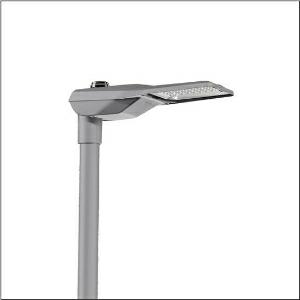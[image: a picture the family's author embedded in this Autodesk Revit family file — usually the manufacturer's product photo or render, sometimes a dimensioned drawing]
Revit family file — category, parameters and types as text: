
# Revit family: streetlight_sl_21_mini___st1_0a_5xe6d47n08gb_0bcc
name_source: partatom
category: Lighting Fixtures
units: mm (PartAtom-declared; Revit-internal decimal feet)

## family parameters
Cut with Voids When Loaded = No
Host = Face
Light Source = No
Part Type = Normal
Room Calculation Point = No
Round Connector Dimension = Use Diameter
Shared = No

## types (1)
- --- (1 x LED, 6180 lm, 40.4 W, 4000K)
    Apparent Load = 40 VA
    CIE Flux Codes = 37 72 97 100 100
    Color Rendering = 70
    Color Temperature = 4000K
    Default Elevation = 1800 mm
    Description = Streetlight SL 21 mini, mast luminaire, primary light control with lens, of PMMA, primary optical cover: cover, of toughened safety glass, transparent, light distribution: ST1.0a, light emission: direct distribution, primary light characteristic: asymmetric, installation type: side-entry, LED, 3G 1.5mm², High Power LED, rated luminous flux: 6.180lm, luminous efficacy: 153lm/W, light colour: 740, colour temperature: 4000K, control gear: NEMA (7pin), control: overheat protection, pre-setting: linear dimming characteristic, constant luminous flux control, time-dependent luminous flux control, flexible luminous flux parameterisation, mains connection: 230..240V, AC, 50/60Hz, connection cable pre-assembled, cable length: 8,5m, wiring characteristics: H07RN-F, start of lifetime: 40W, end of service life: 41W, reduction: 19W, luminaire housing, of diecast aluminium (EN AC-44300), powder-coated, Siteco® metallic grey (DB 702S), corrosivity category C5 mid according to DIN EN ISO 12944, multi-level sealing system, sealing non-destructively replaceable, inclination adjustable: 0°, 5°, 10°, 15°, length: 628mm, width: 235mm, height: 110mm, spigot size: 42mm (side-entry), mounting height: 4..8m, protection rating (complete): IP66, insulation class (complete): insulation class I (protective earthing), certification: CE, ENEC, ENEC+, VDE, impact resistance: IK10, permissible operating ambient temperature for outdoor applications: -40..+50°C, standard-compliant lighting for roads and squares, packaging unit: 1 piece

Light Distribution: ST1.0a
    Height = 110 mm
    Lamp = 1 x LED
    Lamp Light Flux = 6180 lm
    Lamp Power = 40.4 W
    Lamp count = 1
    Length = 625 mm
    Luminous efficacy = 153 lm/W
    Manufacturer = Siteco
    ModVariant = No
    Model = 5XE6D47N08GB
    Number of Poles = 1
    OnlyDefault = Yes
    Power Factor = 1
    Product Name = Streetlight SL 21 mini | ST1.0a
    Product group = mast luminaire | pylon top
    ProductGroupID = 6100
    Protection Class = Protection class I
    Protection Degree = IP 66
    RLX_Detail_Level = 1
    RLX_Emergency_Light_Flux = 0 lm
    RLX_Emergency_Type = 0
    RLX_Emergency_Type_DB = No
    RlxData = <blob elided: 25757 chars, md5=4ca1619c>
    Socket = socket
    Standby Power = 0 W
    System Light Flux = 6180 lm
    System Power = 40 W
    Type Comments = factory setting: luminous flux: 100 % | dim-lin: 254 | 812 mA
    Type Image = l_1294379.jpg
    URL = http://relux.com
    VarID = @adj_157723
    Voltage = 0 V
    Weight = 0.00 kg
    Width = 234 mm

## geometry (parser evidence)
native form markers: Blend x4, Sweep x11
no freeform markers — native parametric forms only
